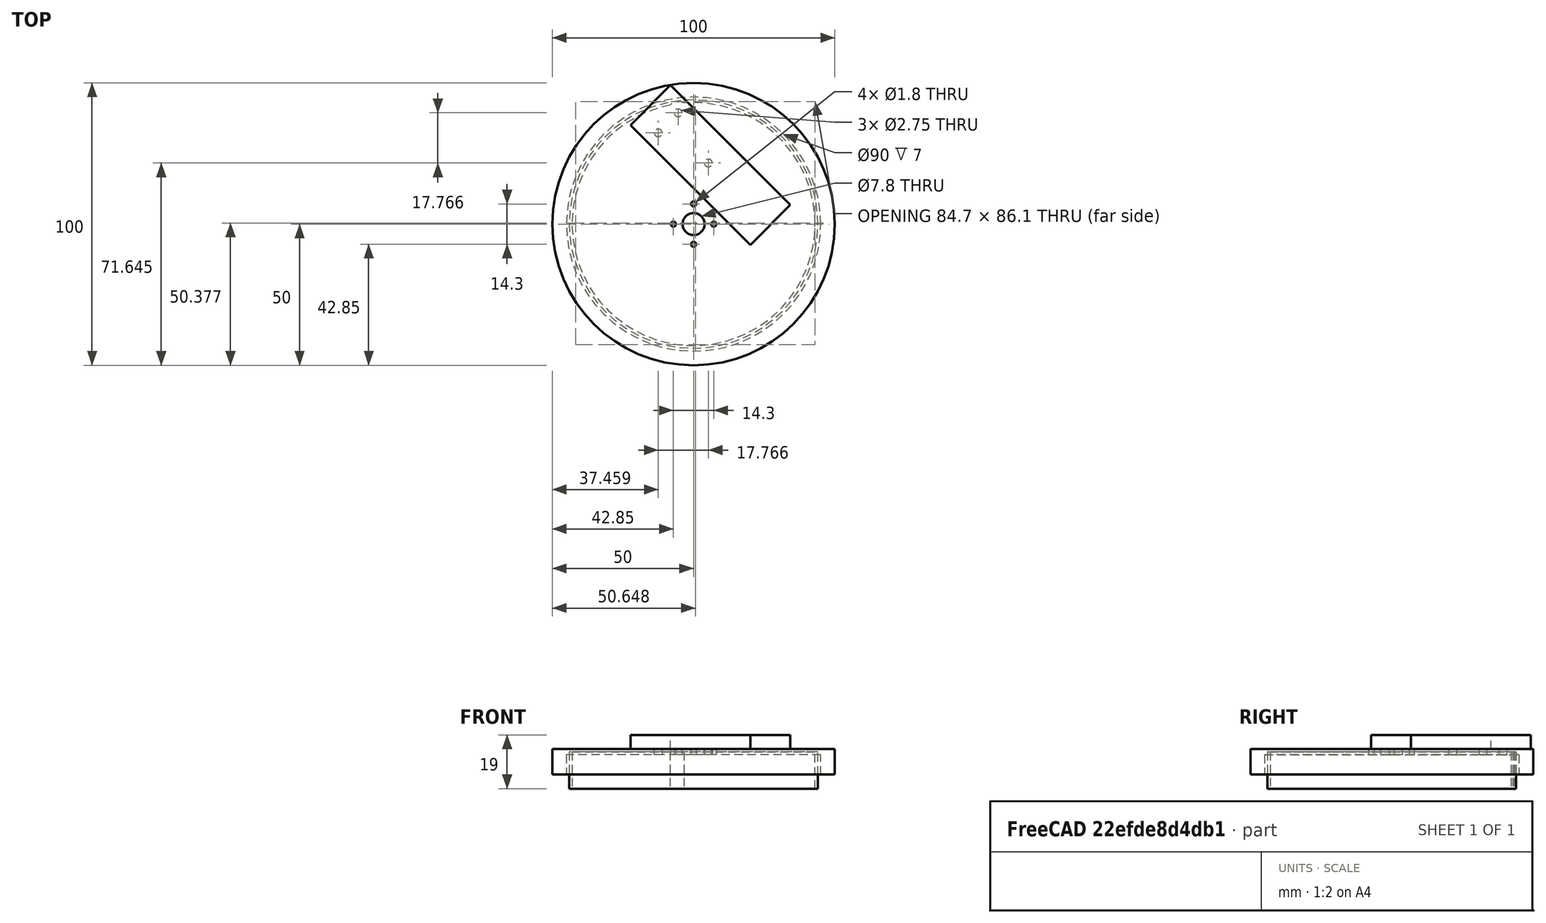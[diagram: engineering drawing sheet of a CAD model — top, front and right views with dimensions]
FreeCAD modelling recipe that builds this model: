
FCSTD DOCUMENT  (FreeCAD 1.0R39109 (Git))
Label: platform
License: All rights reserved
LicenseURL: https://en.wikipedia.org/wiki/All_rights_reserved
objects: Part::Cut×5, Sketcher::SketchObject×5, Part::Extrusion×5, Part::Cylinder×4, Part::MultiFuse×1, Mesh::Feature×1
note: 25 computed .brp shape members not serialized (recipe doc carries the construction recipe); baked Part::Feature solids carry a one-line shape summary decoded from their .brp

FEATURE [Part::Cylinder] Cylinder
  Angle = 360
  AttacherType = Attacher::AttachEngine3D
  FirstAngle = 0
  Height = 9
  Radius = 50
  SecondAngle = 0
FEATURE [Part::Cylinder] Cylinder001
  Angle = 360
  AttacherType = Attacher::AttachEngine3D
  FirstAngle = 0
  Height = 7
  Radius = 45
  SecondAngle = 0
FEATURE [Part::Cut] Cut
  Base = -> Cylinder
  Tool = -> Cylinder001
FEATURE [Sketcher::SketchObject] Sketch  label="Screwholes-middle-inner-sketch"
  ArcFitTolerance = 1e-06
  AttachmentSupport = -> [Cut]
  FullyConstrained = true
  MakeInternals = false
  MapMode = 5
  Placement = pos=(0,0,9) rot=(0,0,1;0rad)
  sketch-geometry (1):
    g0: Circle CenterX=0 CenterY=0 CenterZ=0 NormalX=0 NormalY=0 NormalZ=1 AngleXU=0 Radius=3.9
  constraints (2):
    c: Coincident(g0,g-1)
    c: Diameter(g0) = 7.8
FEATURE [Part::Extrusion] Extrude001  label="Screwholes-middle-inner"
  Base = -> Sketch
  Dir = (0,0,1)
  DirMode = 2
  FaceMakerClass = Part::FaceMakerBullseye
  FaceMakerMode = 3
  LengthFwd = -2
  LengthRev = 0
  Solid = true
  Symmetric = false
FEATURE [Part::Cut] Cut001
  Base = -> Cut
  Tool = -> Extrude001
FEATURE [Sketcher::SketchObject] Sketch001  label="Screwholes-middle-outer-sketch"
  ArcFitTolerance = 1e-06
  AttachmentSupport = -> [Cut001]
  FullyConstrained = true
  MakeInternals = false
  MapMode = 5
  Placement = pos=(0,0,9) rot=(0,0,1;0rad)
  sketch-geometry (4):
    g0: Circle CenterX=0 CenterY=7.15 CenterZ=0 NormalX=0 NormalY=0 NormalZ=1 AngleXU=0 Radius=0.9
    g1: Circle CenterX=-7.15 CenterY=0 CenterZ=0 NormalX=0 NormalY=0 NormalZ=1 AngleXU=0 Radius=0.9
    g2: Circle CenterX=0 CenterY=-7.15 CenterZ=0 NormalX=0 NormalY=0 NormalZ=1 AngleXU=0 Radius=0.9
    g3: Circle CenterX=7.15 CenterY=0 CenterZ=0 NormalX=0 NormalY=0 NormalZ=1 AngleXU=0 Radius=0.9
  constraints (12):
    c: PointOnObject(g0,g-2)
    c: DistanceY(g-1,g0) = 7.15
    c: PointOnObject(g1,g-1)
    c: PointOnObject(g2,g-2)
    c: PointOnObject(g3,g-1)
    c: Equal(g0,g1)
    c: Equal(g1,g2)
    c: Equal(g2,g3)
    c: DistanceX(g1,g-1) = 7.15
    c: DistanceY(g2,g-1) = 7.15
    c: DistanceX(g-1,g3) = 7.15
    c: Diameter(g1) = 1.8
FEATURE [Part::Extrusion] Extrude  label="Screwholes-middle-outer"
  Base = -> Sketch001
  Dir = (0,0,1)
  DirMode = 2
  FaceMakerClass = Part::FaceMakerBullseye
  FaceMakerMode = 3
  LengthFwd = -2
  LengthRev = 0
  Solid = true
  Symmetric = false
FEATURE [Part::Cut] Cut002  label="platform-middle-screwholes"
  Base = -> Cut001
  Tool = -> Extrude
FEATURE [Sketcher::SketchObject] Sketch002
  ArcFitTolerance = 1e-06
  AttachmentSupport = -> [Cut002]
  ExternalGeometry = -> [Cut002]
  FullyConstrained = true
  MakeInternals = false
  MapMode = 5
  Placement = pos=(0,0,9) rot=(0,0,1;0rad)
  sketch-geometry (4):
    g0: LineSegment StartX=-22.3521 StartY=35.0801 StartZ=0 EndX=20.0743 EndY=-7.34635 EndZ=0
    g1: LineSegment StartX=20.0743 StartY=-7.34635 StartZ=0 EndX=34.2164 EndY=6.79579 EndZ=0
    g2: LineSegment StartX=34.2164 StartY=6.79579 StartZ=0 EndX=-8.21 EndY=49.2222 EndZ=0
    g3: LineSegment StartX=-8.21 StartY=49.2222 StartZ=0 EndX=-22.3521 EndY=35.0801 EndZ=0
  constraints (12):
    c: Coincident(g0,g1)
    c: Coincident(g1,g2)
    c: Coincident(g2,g3)
    c: Coincident(g3,g0)
    c: Angle(g3,g2) = 1.5708
    c: Angle(g2,g1) = 1.5708
    c: Angle(g0,g3) = 1.5708
    c: Distance(g0,g1) = 20
    c: Distance(g0) = 60
    c: Distance(g-1,g0) = 9
    c: DistanceX(g-2,g2) = -8.21
    c: Angle(g0,g-1) = 0.785398
FEATURE [Part::Extrusion] Extrude002  label="shoulder-outline"
  Base = -> Sketch002
  Dir = (0,0,1)
  DirMode = 2
  FaceMakerClass = Part::FaceMakerBullseye
  FaceMakerMode = 3
  LengthFwd = 5
  LengthRev = 0
  Solid = true
  Symmetric = false
FEATURE [Sketcher::SketchObject] Sketch003
  ArcFitTolerance = 1e-06
  AttachmentSupport = -> [Extrude002]
  ExternalGeometry = -> [Extrude002]
  FullyConstrained = true
  MakeInternals = false
  MapMode = 5
  Placement = pos=(0,0,14) rot=(0,0,1;0rad)
  sketch-geometry (3):
    g0: Circle CenterX=-12.541 CenterY=32.34 CenterZ=0 NormalX=0 NormalY=0 NormalZ=1 AngleXU=0 Radius=1.375
    g1: Circle CenterX=-5.46996 CenterY=39.4111 CenterZ=0 NormalX=0 NormalY=0 NormalZ=1 AngleXU=0 Radius=1.375
    g2: Circle CenterX=5.22503 CenterY=21.645 CenterZ=0 NormalX=0 NormalY=0 NormalZ=1 AngleXU=0 Radius=1.375
  constraints (9):
    c: Diameter(g0) = 2.75
    c: Distance(g0,g-3) = 8.875
    c: Distance(g0,g-4) = 5
    c: Equal(g0,g1)
    c: Distance(g1,g-5) = 5
    c: Distance(g1,g-3) = 8.875
    c: Diameter(g2) = 2.75
    c: Distance(g2,g-5) = 10
    c: Distance(g2,g-6) = 31
FEATURE [Part::Extrusion] Extrude004
  Base = -> Sketch003
  Dir = (0,0,1)
  DirMode = 2
  FaceMakerClass = Part::FaceMakerBullseye
  FaceMakerMode = 3
  LengthFwd = -10
  LengthRev = 0
  Solid = true
  Symmetric = false
FEATURE [Part::Cut] Cut003  label="platform-shoulder-screws"
  Base = -> Cut002
  Tool = -> Extrude004
FEATURE [Sketcher::SketchObject] Sketch006
  ArcFitTolerance = 1e-06
  FullyConstrained = true
  MakeInternals = false
  MapMode = 2
  sketch-geometry (1):
    g0: Circle CenterX=-5.45 CenterY=39.43 CenterZ=0 NormalX=0 NormalY=0 NormalZ=1 AngleXU=0 Radius=4
  constraints (3):
    c: Diameter(g0) = 8
    c: DistanceX(g0,g-1) = 5.45
    c: DistanceY(g-1,g0) = 39.43
FEATURE [Part::Extrusion] Extrude008
  Base = -> Sketch006
  Dir = (0,0,1)
  DirMode = 2
  FaceMakerClass = Part::FaceMakerBullseye
  FaceMakerMode = 3
  LengthFwd = 13
  LengthRev = 0
  Placement = pos=(0,0,-5) rot=(0,0,1;0rad)
  Solid = true
  Symmetric = false
FEATURE [Part::Cylinder] Cylinder002  label="overlap"
  Angle = 360
  AttacherType = Attacher::AttachEngine3D
  FirstAngle = 0
  Height = 13
  Placement = pos=(0,0,-5) rot=(0,0,1;0rad)
  Radius = 44
  SecondAngle = 0
FEATURE [Part::Cylinder] Cylinder003
  Angle = 360
  AttacherType = Attacher::AttachEngine3D
  FirstAngle = 0
  Height = 13
  Placement = pos=(0,0,-5) rot=(0,0,1;0rad)
  Radius = 43
  SecondAngle = 0
FEATURE [Part::MultiFuse] Fusion  label="overlap-cutout"
  Shapes = -> [Cylinder003,Extrude008]
FEATURE [Part::Cut] Cut006  label="overlap-with-cutout"
  Base = -> Cylinder002
  Tool = -> Fusion
FEATURE [Mesh::Feature] Mesh  label="platform-shoulder-screws (Meshed)"
